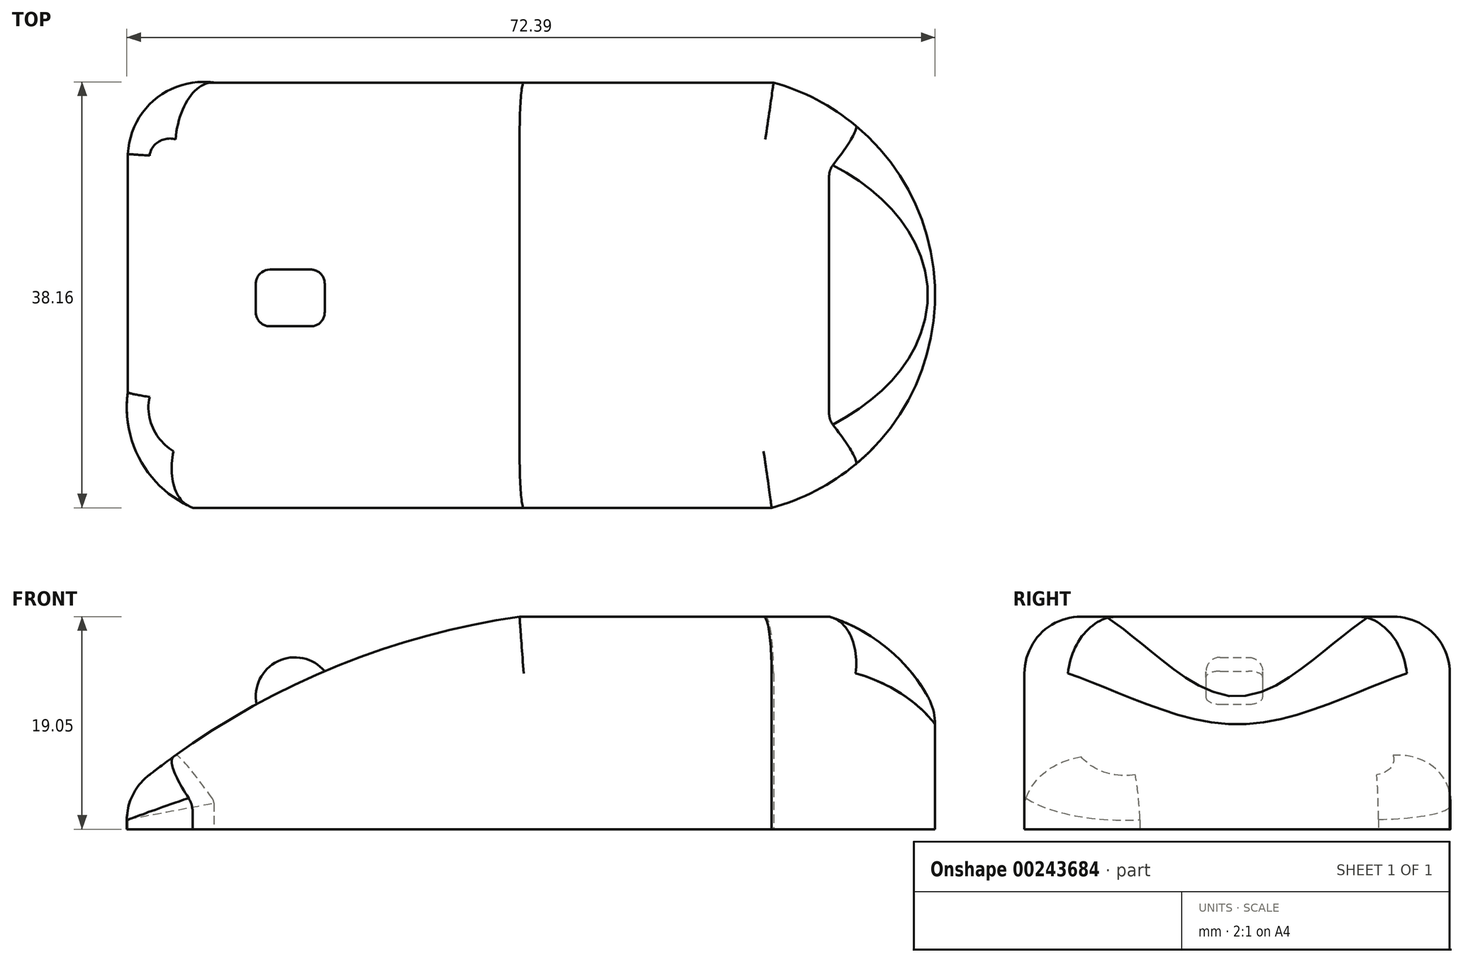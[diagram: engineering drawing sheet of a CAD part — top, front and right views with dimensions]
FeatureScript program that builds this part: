
annotation { "Feature Type Name" : "Feature", "Feature Type Description" : "" }
export const myFeature = defineFeature(function(context is Context, id is Id, definition is map)
    precondition{}
    {
        {
            var Q0;
            Q0=qCreatedBy(makeId("Top.planeOp"),FACE);
            var sketch = newSketch(context, id + "F0", { "sketchPlane" : qUnion([Q0])});
            skLineSegment(sketch, "E0.bottom", {"start": v(-31.07, -1.02) * mm, "end": v(20.93, -1.02) * mm});
            skLineSegment(sketch, "E0.top", {"start": v(-31.1, -39.12) * mm, "end": v(20.76, -39.12) * mm});
            skLineSegment(sketch, "E0.left", {"start": v(-36.9, -7.4) * mm, "end": v(-36.9, -31.55) * mm});
            skArc(sketch, "E1", {"start": v(20.76, -39.12) * mm, "mid": v(35.4, -20.14) * mm, "end": v(20.93, -1.02) * mm});
            skArc(sketch, "E2", {"start": v(-36.9, -28.77) * mm, "mid": v(-35.75, -34.93) * mm, "end": v(-31.1, -39.12) * mm});
            skArc(sketch, "E3", {"start": v(-29.2, -1.02) * mm, "mid": v(-34.45, -2.52) * mm, "end": v(-36.9, -7.4) * mm});
            skSolve(sketch);
        }
        {
            var Q0;
            Q0 = qSketchRegion(id + "F0", true);
            extrude(context, id + "F1", {"entities" : qUnion([Q0]), "depth" : 19.05 * mm});
        }
        {
            var Q0;
            Q0=qCreatedBy(makeId("Front.planeOp"),FACE);
            var sketch = newSketch(context, id + "F2", { "sketchPlane" : qUnion([Q0])});
            skLineSegment(sketch, "E4.bottom", {"start": v(-37.14, 19.74) * mm, "end": v(36.15, 19.74) * mm});
            skLineSegment(sketch, "E4.top", {"start": v(-37.14, 0) * mm, "end": v(36.15, 0) * mm});
            skLineSegment(sketch, "E4.left", {"start": v(-37.14, 19.74) * mm, "end": v(-37.14, 0) * mm});
            skLineSegment(sketch, "E4.right", {"start": v(36.15, 19.74) * mm, "end": v(36.15, 0) * mm});
            skArc(sketch, "E5", {"start": v(6.22, 19.74) * mm, "mid": v(-16.88, 15.12) * mm, "end": v(-37.14, 3.1) * mm});
            skArc(sketch, "E6", {"start": v(36.15, 8.52) * mm, "mid": v(30.87, 16.42) * mm, "end": v(21.96, 19.74) * mm});
            skSolve(sketch);
        }
        {
            var Q0;
            {var subQ3=sQuery(id+"F2.wireOp",EDGE,"E6");Q0=makeQuery(id+"F2.imprint","IMPRINT",FACE,{"disambiguationData":[TD([[makeQuery(id+"F2.imprint","IMPRINT",EDGE,{"derivedFrom":subQ3}),-1.0]])]});}
            var Q1;
            {var subQ3=sQuery(id+"F2.wireOp",EDGE,"E5");Q1=makeQuery(id+"F2.imprint","IMPRINT",FACE,{"disambiguationData":[TD([[makeQuery(id+"F2.imprint","IMPRINT",EDGE,{"derivedFrom":subQ3}),-1.0]])]});}
            extrude(context, id + "F3", {"entities" : qUnion([Q0, Q1]), "operationType" : NewBodyOperationType.REMOVE, "depth" : 50.8 * mm});
        }
        {
            var Q0;
            Q0=qCreatedBy(makeId("Front.planeOp"),FACE);
            cPlane(context, id + "F4", {"entities" : qUnion([Q0]), "cplaneType" : CPlaneType.OFFSET, "offset" : 20.32 * mm, "width" : 152.4 * mm, "height" : 152.4 * mm});
        }
        {
            var Q0;
            Q0=qCreatedBy(id+"F4.planeOp",FACE);
            var sketch = newSketch(context, id + "F5", { "sketchPlane" : qUnion([Q0])});
            skCircle(sketch, "E7", {"center": v(-21.94, 11.9) * mm, "radius": 3.5 * mm});
            skSolve(sketch);
        }
        {
            var Q0;
            Q0 = qSketchRegion(id + "F5", true);
            extrude(context, id + "F6", {"entities" : qUnion([Q0]), "operationType" : NewBodyOperationType.ADD, "depth" : 2.54 * mm, "hasSecondDirection" : true, "secondDirectionOppositeDirection" : true, "secondDirectionDepth" : 2.54 * mm});
        }
        {
            var Q0;
            Q0=makeQuery(id+"F3.boolean.opBoolean","INTERSECT",EDGE,{"derivedFrom":[makeQuery(id+"F1.opExtrude","SWEPT_FACE",FACE,{"disambiguationData":[OSD([sQuery(id+"F0.wireOp",EDGE,"E0.top")])]}),makeQuery(id+"F3.opExtrude","SWEPT_FACE",FACE,{"disambiguationData":[OSD([sQuery(id+"F2.wireOp",EDGE,"E5")])]})]});
            var Q1;
            Q1=makeQuery(id+"F1.opExtrude","CAP_EDGE",EDGE,{"disambiguationData":[OSD([sQuery(id+"F0.wireOp",EDGE,"E0.top")])],"isStart":false});
            var Q2;
            Q2=makeQuery(id+"F3.boolean.opBoolean","INTERSECT",EDGE,{"derivedFrom":[makeQuery(id+"F1.opExtrude","SWEPT_FACE",FACE,{"disambiguationData":[OSD([sQuery(id+"F0.wireOp",EDGE,"E2")])]}),makeQuery(id+"F3.opExtrude","SWEPT_FACE",FACE,{"disambiguationData":[OSD([sQuery(id+"F2.wireOp",EDGE,"E5")])]})]});
            var Q3;
            Q3=makeQuery(id+"F3.boolean.opBoolean","INTERSECT",EDGE,{"derivedFrom":[makeQuery(id+"F1.opExtrude","SWEPT_FACE",FACE,{"disambiguationData":[OSD([sQuery(id+"F0.wireOp",EDGE,"E0.left")])]}),makeQuery(id+"F3.opExtrude","SWEPT_FACE",FACE,{"disambiguationData":[OSD([sQuery(id+"F2.wireOp",EDGE,"E5")])]})]});
            var Q4;
            Q4=makeQuery(id+"F3.boolean.opBoolean","INTERSECT",EDGE,{"derivedFrom":[makeQuery(id+"F1.opExtrude","SWEPT_FACE",FACE,{"disambiguationData":[OSD([sQuery(id+"F0.wireOp",EDGE,"E3")])]}),makeQuery(id+"F3.opExtrude","SWEPT_FACE",FACE,{"disambiguationData":[OSD([sQuery(id+"F2.wireOp",EDGE,"E5")])]})]});
            var Q5;
            Q5=makeQuery(id+"F3.boolean.opBoolean","INTERSECT",EDGE,{"derivedFrom":[makeQuery(id+"F1.opExtrude","SWEPT_FACE",FACE,{"disambiguationData":[OSD([sQuery(id+"F0.wireOp",EDGE,"E0.bottom")])]}),makeQuery(id+"F3.opExtrude","SWEPT_FACE",FACE,{"disambiguationData":[OSD([sQuery(id+"F2.wireOp",EDGE,"E5")])]})]});
            var Q6;
            Q6=makeQuery(id+"F1.opExtrude","CAP_EDGE",EDGE,{"disambiguationData":[OSD([sQuery(id+"F0.wireOp",EDGE,"E0.bottom")])],"isStart":false});
            var Q7;
            {var subQ0=sQuery(id+"F0.wireOp",EDGE,"E0.bottom");var subQ1=sQuery(id+"F0.wireOp",EDGE,"E1");Q7=makeQuery(id+"F3.boolean.opBoolean","SPLIT",EDGE,{"disambiguationData":[TD([makeQuery(id+"F1.opExtrude","SWEPT_FACE",FACE,{"disambiguationData":[OSD([subQ0])]})])],"derivedFrom":makeQuery(id+"F1.opExtrude","CAP_EDGE",EDGE,{"disambiguationData":[OSD([subQ1])],"isStart":false})});}
            var Q8;
            Q8=makeQuery(id+"F3.boolean.opBoolean","INTERSECT",EDGE,{"derivedFrom":[makeQuery(id+"F1.opExtrude","SWEPT_FACE",FACE,{"disambiguationData":[OSD([sQuery(id+"F0.wireOp",EDGE,"E1")])]}),makeQuery(id+"F3.opExtrude","SWEPT_FACE",FACE,{"disambiguationData":[OSD([sQuery(id+"F2.wireOp",EDGE,"E6")])]})]});
            var Q9;
            {var subQ0=sQuery(id+"F0.wireOp",EDGE,"E1");var subQ1=sQuery(id+"F0.wireOp",EDGE,"E0.top");Q9=makeQuery(id+"F3.boolean.opBoolean","SPLIT",EDGE,{"disambiguationData":[TD([makeQuery(id+"F1.opExtrude","SWEPT_FACE",FACE,{"disambiguationData":[OSD([subQ1])]})])],"derivedFrom":makeQuery(id+"F1.opExtrude","CAP_EDGE",EDGE,{"disambiguationData":[OSD([subQ0])],"isStart":false})});}
            fillet(context, id + "F7", {"entities" : qUnion([Q0, Q1, Q2, Q3, Q4, Q5, Q6, Q7, Q8, Q9]), "radius" : 5.08 * mm, "tangentPropagation" : true, "allowEdgeOverflow" : false});
        }
        {
            var Q0;
            Q0=makeQuery(id+"F6.opExtrude","CAP_EDGE",EDGE,{"disambiguationData":[OSD([sQuery(id+"F5.wireOp",EDGE,"E7")])],"isStart":false});
            var Q1;
            Q1=makeQuery(id+"F6.opExtrude","CAP_EDGE",EDGE,{"disambiguationData":[OSD([sQuery(id+"F5.wireOp",EDGE,"E7")])],"isStart":true});
            fillet(context, id + "F8", {"entities" : qUnion([Q0, Q1]), "radius" : 1.27 * mm, "tangentPropagation" : true, "allowEdgeOverflow" : false});
        }
    });
